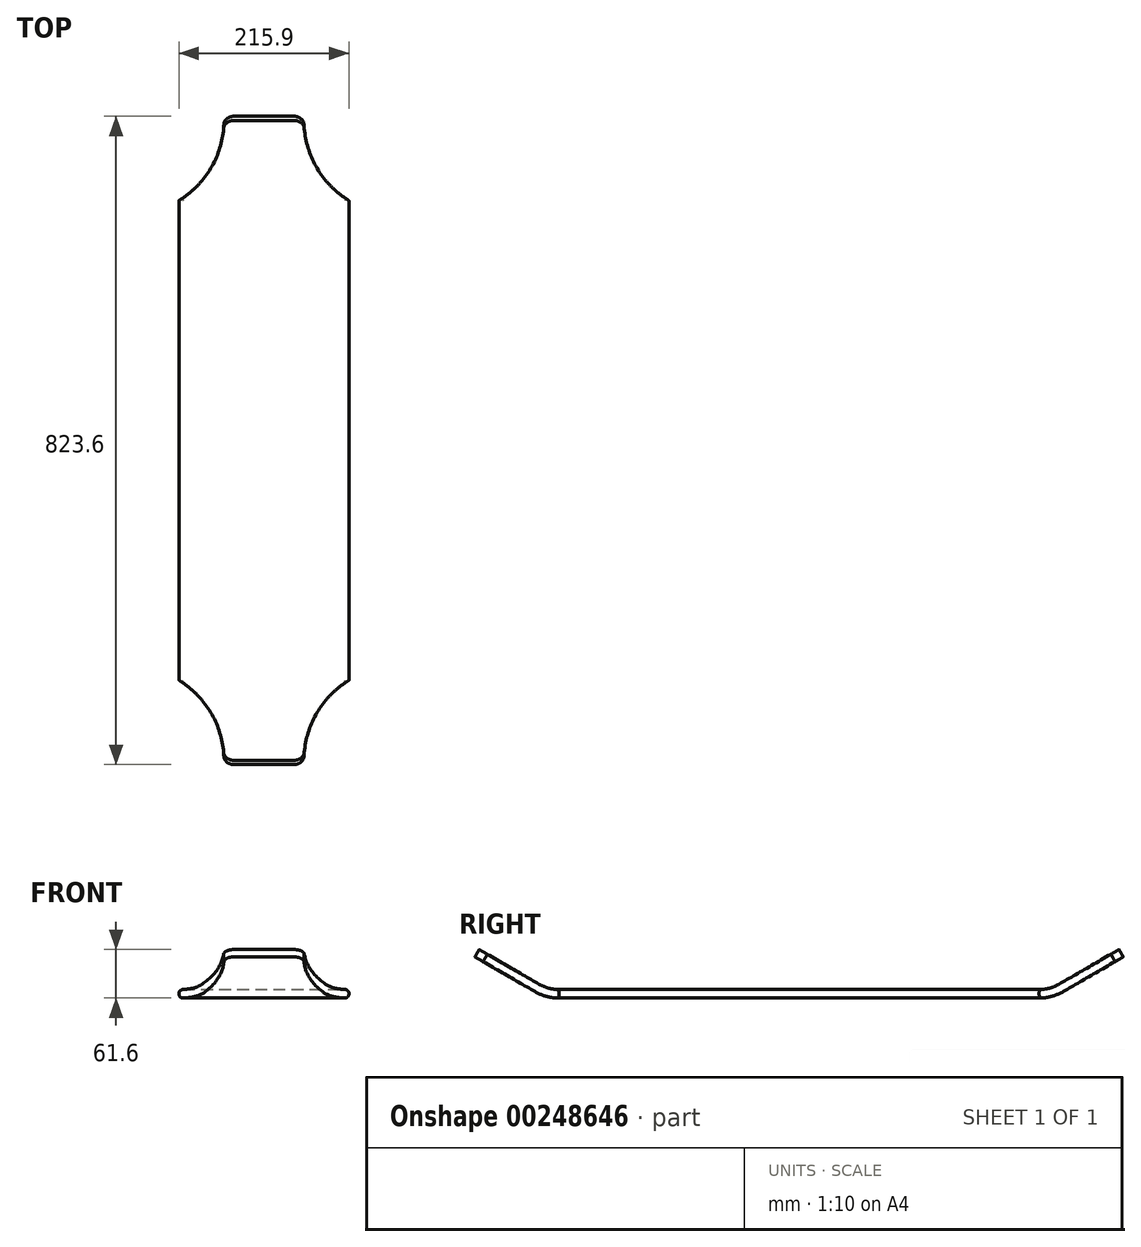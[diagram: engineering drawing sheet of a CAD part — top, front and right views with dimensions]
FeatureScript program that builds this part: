
annotation { "Feature Type Name" : "Feature", "Feature Type Description" : "" }
export const myFeature = defineFeature(function(context is Context, id is Id, definition is map)
    precondition{}
    {
        {
            var Q0;
            Q0=qCreatedBy(makeId("Right.planeOp"),FACE);
            var sketch = newSketch(context, id + "F0", { "sketchPlane" : qUnion([Q0])});
            skLineSegment(sketch, "E0", {"start": v(101.6, -50.8) * mm, "end": v(711.2, -50.8) * mm});
            skLineSegment(sketch, "E1", {"start": v(406.4, -50.8) * mm, "end": v(406.4, 132.37) * mm, "construction": true});
            skLineSegment(sketch, "E2.1", {"start": v(101.6, -61.6) * mm, "end": v(711.2, -61.6) * mm});
            skLineSegment(sketch, "E3", {"start": v(0, 0) * mm, "end": v(-5.4, -9.35) * mm});
            skLineSegment(sketch, "E4", {"start": v(812.8, 0) * mm, "end": v(818.2, -9.35) * mm});
            skLineSegment(sketch, "E5", {"start": v(0, 0) * mm, "end": v(76.2, -44) * mm});
            skLineSegment(sketch, "E6", {"start": v(-5.4, -9.35) * mm, "end": v(70.8, -53.34) * mm});
            skPoint(sketch, "E7.visualSharp", {"position": v(87.99, -50.8) * mm});
            skArc(sketch, "E7.filletArc", {"start": v(76.2, -44) * mm, "mid": v(88.45, -49.07) * mm, "end": v(101.6, -50.8) * mm});
            skPoint(sketch, "E8.visualSharp", {"position": v(85.1, -61.6) * mm});
            skArc(sketch, "E8.filletArc", {"start": v(70.8, -53.34) * mm, "mid": v(85.66, -59.5) * mm, "end": v(101.6, -61.6) * mm});
            skLineSegment(sketch, "E9", {"start": v(812.8, 0) * mm, "end": v(736.6, -44) * mm});
            skLineSegment(sketch, "E10", {"start": v(818.2, -9.35) * mm, "end": v(742, -53.34) * mm});
            skPoint(sketch, "E11.visualSharp", {"position": v(724.81, -50.8) * mm});
            skArc(sketch, "E11.filletArc", {"start": v(711.2, -50.8) * mm, "mid": v(724.35, -49.07) * mm, "end": v(736.6, -44) * mm});
            skPoint(sketch, "E12.visualSharp", {"position": v(727.7, -61.6) * mm});
            skArc(sketch, "E12.filletArc", {"start": v(711.2, -61.6) * mm, "mid": v(727.14, -59.5) * mm, "end": v(742, -53.34) * mm});
            skSolve(sketch);
        }
        {
            var Q0;
            Q0 = qSketchRegion(id + "F0", true);
            extrude(context, id + "F1", {"entities" : qUnion([Q0]), "oppositeDirection" : true, "depth" : 215.9 * mm});
        }
        {
            var Q0;
            Q0=qCreatedBy(makeId("Top.planeOp"),FACE);
            var sketch = newSketch(context, id + "F2", { "sketchPlane" : qUnion([Q0])});
            skLineSegment(sketch, "E13.bottom", {"start": v(-280.25, -135.54) * mm, "end": v(-158.75, -135.54) * mm});
            skLineSegment(sketch, "E13.top", {"start": v(-280.25, 101.6) * mm, "end": v(-215.9, 101.6) * mm});
            skLineSegment(sketch, "E13.left", {"start": v(-280.25, -135.54) * mm, "end": v(-280.25, 101.6) * mm});
            skLineSegment(sketch, "E13.right", {"start": v(-158.75, -135.54) * mm, "end": v(-158.75, 0) * mm});
            skLineSegment(sketch, "E14", {"start": v(-107.95, 0) * mm, "end": v(-107.95, 235.99) * mm, "construction": true});
            skLineSegment(sketch, "E15.0", {"start": v(-215.9, 101.6) * mm, "end": v(-215.9, 711.2) * mm, "construction": true});
            skPoint(sketch, "E16.orphan", {"position": v(-215.9, 101.6) * mm});
            skArc(sketch, "E17", {"start": v(-158.75, 0) * mm, "mid": v(-174.02, 58.29) * mm, "end": v(-215.9, 101.6) * mm});
            skLineSegment(sketch, "E18", {"start": v(-215.9, 406.4) * mm, "end": v(90.88, 406.4) * mm, "construction": true});
            skPoint(sketch, "E19.MirrorP", {"position": v(0, 101.6) * mm});
            skLineSegment(sketch, "E20.MirrorCS", {"start": v(64.35, -135.54) * mm, "end": v(-57.15, -135.54) * mm});
            skLineSegment(sketch, "E21.MirrorCS", {"start": v(64.35, 101.6) * mm, "end": v(0, 101.6) * mm});
            skLineSegment(sketch, "E22.MirrorCS", {"start": v(64.35, -135.54) * mm, "end": v(64.35, 101.6) * mm});
            skLineSegment(sketch, "E23.MirrorCS", {"start": v(-57.15, -135.54) * mm, "end": v(-57.15, 0) * mm});
            skArc(sketch, "E24.MirrorCS", {"start": v(-57.15, 0) * mm, "mid": v(-41.88, 58.29) * mm, "end": v(0, 101.6) * mm});
            skLineSegment(sketch, "E25.MirrorCS", {"start": v(64.35, 948.34) * mm, "end": v(64.35, 711.2) * mm});
            skLineSegment(sketch, "E26.MirrorCS", {"start": v(-280.25, 948.34) * mm, "end": v(-158.75, 948.34) * mm});
            skLineSegment(sketch, "E27.MirrorCS", {"start": v(-280.25, 711.2) * mm, "end": v(-215.9, 711.2) * mm});
            skLineSegment(sketch, "E28.MirrorCS", {"start": v(-280.25, 948.34) * mm, "end": v(-280.25, 711.2) * mm});
            skArc(sketch, "E29.MirrorCS", {"start": v(-158.75, 812.8) * mm, "mid": v(-174.02, 754.51) * mm, "end": v(-215.9, 711.2) * mm});
            skArc(sketch, "E30.MirrorCS", {"start": v(-57.15, 812.8) * mm, "mid": v(-41.88, 754.51) * mm, "end": v(0, 711.2) * mm});
            skPoint(sketch, "E31.MirrorP", {"position": v(-215.9, 711.2) * mm});
            skLineSegment(sketch, "E32.MirrorCS", {"start": v(-158.75, 948.34) * mm, "end": v(-158.75, 812.8) * mm});
            skLineSegment(sketch, "E33.MirrorCS", {"start": v(64.35, 948.34) * mm, "end": v(-57.15, 948.34) * mm});
            skLineSegment(sketch, "E34.MirrorCS", {"start": v(64.35, 711.2) * mm, "end": v(0, 711.2) * mm});
            skPoint(sketch, "E35.MirrorP", {"position": v(0, 711.2) * mm});
            skLineSegment(sketch, "E36.MirrorCS", {"start": v(-57.15, 948.34) * mm, "end": v(-57.15, 812.8) * mm});
            skSolve(sketch);
        }
        {
            var Q0;
            Q0 = qSketchRegion(id + "F2", true);
            extrude(context, id + "F3", {"entities" : qUnion([Q0]), "operationType" : NewBodyOperationType.REMOVE, "endBound" : BoundingType.THROUGH_ALL, "oppositeDirection" : true, "depth" : 25.4 * mm});
        }
        {
            var Q0;
            Q0=makeQuery(id+"F3.boolean.opBoolean","INTERSECT",EDGE,{"derivedFrom":[makeQuery(id+"F1.opExtrude","SWEPT_FACE",FACE,{"disambiguationData":[OSD([sQuery(id+"F0.wireOp",EDGE,"E3")])]}),makeQuery(id+"F3.opExtrude","SWEPT_FACE",FACE,{"disambiguationData":[OSD([sQuery(id+"F2.wireOp",EDGE,"E23.MirrorCS")])]})]});
            var Q1;
            Q1=makeQuery(id+"F3.boolean.opBoolean","COPY",EDGE,{"derivedFrom":makeQuery(id+"F3.opExtrude","SWEPT_EDGE",EDGE,{"disambiguationData":[OSD([sQuery(id+"F2.wireOp",EDGE,"E21.MirrorCS"),sQuery(id+"F2.wireOp",EDGE,"E24.MirrorCS")])]})});
            var Q2;
            Q2=makeQuery(id+"F3.boolean.opBoolean","INTERSECT",EDGE,{"derivedFrom":[makeQuery(id+"F1.opExtrude","SWEPT_FACE",FACE,{"disambiguationData":[OSD([sQuery(id+"F0.wireOp",EDGE,"E3")])]}),makeQuery(id+"F3.opExtrude","SWEPT_FACE",FACE,{"disambiguationData":[OSD([sQuery(id+"F2.wireOp",EDGE,"E13.right")])]})]});
            var Q3;
            Q3=makeQuery(id+"F3.boolean.opBoolean","COPY",EDGE,{"derivedFrom":makeQuery(id+"F3.opExtrude","SWEPT_EDGE",EDGE,{"disambiguationData":[OSD([sQuery(id+"F2.wireOp",EDGE,"E13.top"),sQuery(id+"F2.wireOp",EDGE,"E17")])]})});
            var Q4;
            Q4=makeQuery(id+"F3.boolean.opBoolean","INTERSECT",EDGE,{"derivedFrom":[makeQuery(id+"F1.opExtrude","SWEPT_FACE",FACE,{"disambiguationData":[OSD([sQuery(id+"F0.wireOp",EDGE,"E4")])]}),makeQuery(id+"F3.opExtrude","SWEPT_FACE",FACE,{"disambiguationData":[OSD([sQuery(id+"F2.wireOp",EDGE,"E32.MirrorCS")])]})]});
            var Q5;
            Q5=makeQuery(id+"F3.boolean.opBoolean","COPY",EDGE,{"derivedFrom":makeQuery(id+"F3.opExtrude","SWEPT_EDGE",EDGE,{"disambiguationData":[OSD([sQuery(id+"F2.wireOp",EDGE,"E27.MirrorCS"),sQuery(id+"F2.wireOp",EDGE,"E29.MirrorCS")])]})});
            var Q6;
            Q6=makeQuery(id+"F3.boolean.opBoolean","INTERSECT",EDGE,{"derivedFrom":[makeQuery(id+"F1.opExtrude","SWEPT_FACE",FACE,{"disambiguationData":[OSD([sQuery(id+"F0.wireOp",EDGE,"E4")])]}),makeQuery(id+"F3.opExtrude","SWEPT_FACE",FACE,{"disambiguationData":[OSD([sQuery(id+"F2.wireOp",EDGE,"E36.MirrorCS")])]})]});
            var Q7;
            Q7=makeQuery(id+"F3.boolean.opBoolean","COPY",EDGE,{"derivedFrom":makeQuery(id+"F3.opExtrude","SWEPT_EDGE",EDGE,{"disambiguationData":[OSD([sQuery(id+"F2.wireOp",EDGE,"E30.MirrorCS"),sQuery(id+"F2.wireOp",EDGE,"E34.MirrorCS")])]})});
            fillet(context, id + "F4", {"entities" : qUnion([Q0, Q1, Q2, Q3, Q4, Q5, Q6, Q7]), "radius" : 12.7 * mm, "tangentPropagation" : true, "allowEdgeOverflow" : false});
        }
        {
            var Q0;
            Q0=makeQuery(id+"F1.opExtrude","SWEPT_FACE",FACE,{"disambiguationData":[OSD([sQuery(id+"F0.wireOp",EDGE,"Clpd3ZYG-gYaw-rO0R-0Den-WmtYPhrUdRe9")])]});
            var Q1;
            Q1=makeQuery(id+"F1.opExtrude","SWEPT_FACE",FACE,{"disambiguationData":[OSD([sQuery(id+"F0.wireOp",EDGE,"E0")])]});
            var Q2;
            Q2=makeQuery(id+"F1.opExtrude","SWEPT_FACE",FACE,{"disambiguationData":[OSD([sQuery(id+"F0.wireOp",EDGE,"29957753-59a9-4de1-aee8-7bd49e2201f10.MirrorCS")])]});
            var Q3;
            Q3=makeQuery(id+"F1.opExtrude","SWEPT_FACE",FACE,{"disambiguationData":[OSD([sQuery(id+"F0.wireOp",EDGE,"E2.2")])]});
            var Q4;
            Q4=makeQuery(id+"F1.opExtrude","SWEPT_FACE",FACE,{"disambiguationData":[OSD([sQuery(id+"F0.wireOp",EDGE,"E2.1")])]});
            var Q5;
            Q5=makeQuery(id+"F1.opExtrude","SWEPT_FACE",FACE,{"disambiguationData":[OSD([sQuery(id+"F0.wireOp",EDGE,"E2.0")])]});
            fillet(context, id + "F5", {"entities" : qUnion([Q0, Q1, Q2, Q3, Q4, Q5]), "radius" : 5.08 * mm, "tangentPropagation" : true, "allowEdgeOverflow" : false});
        }
    });
